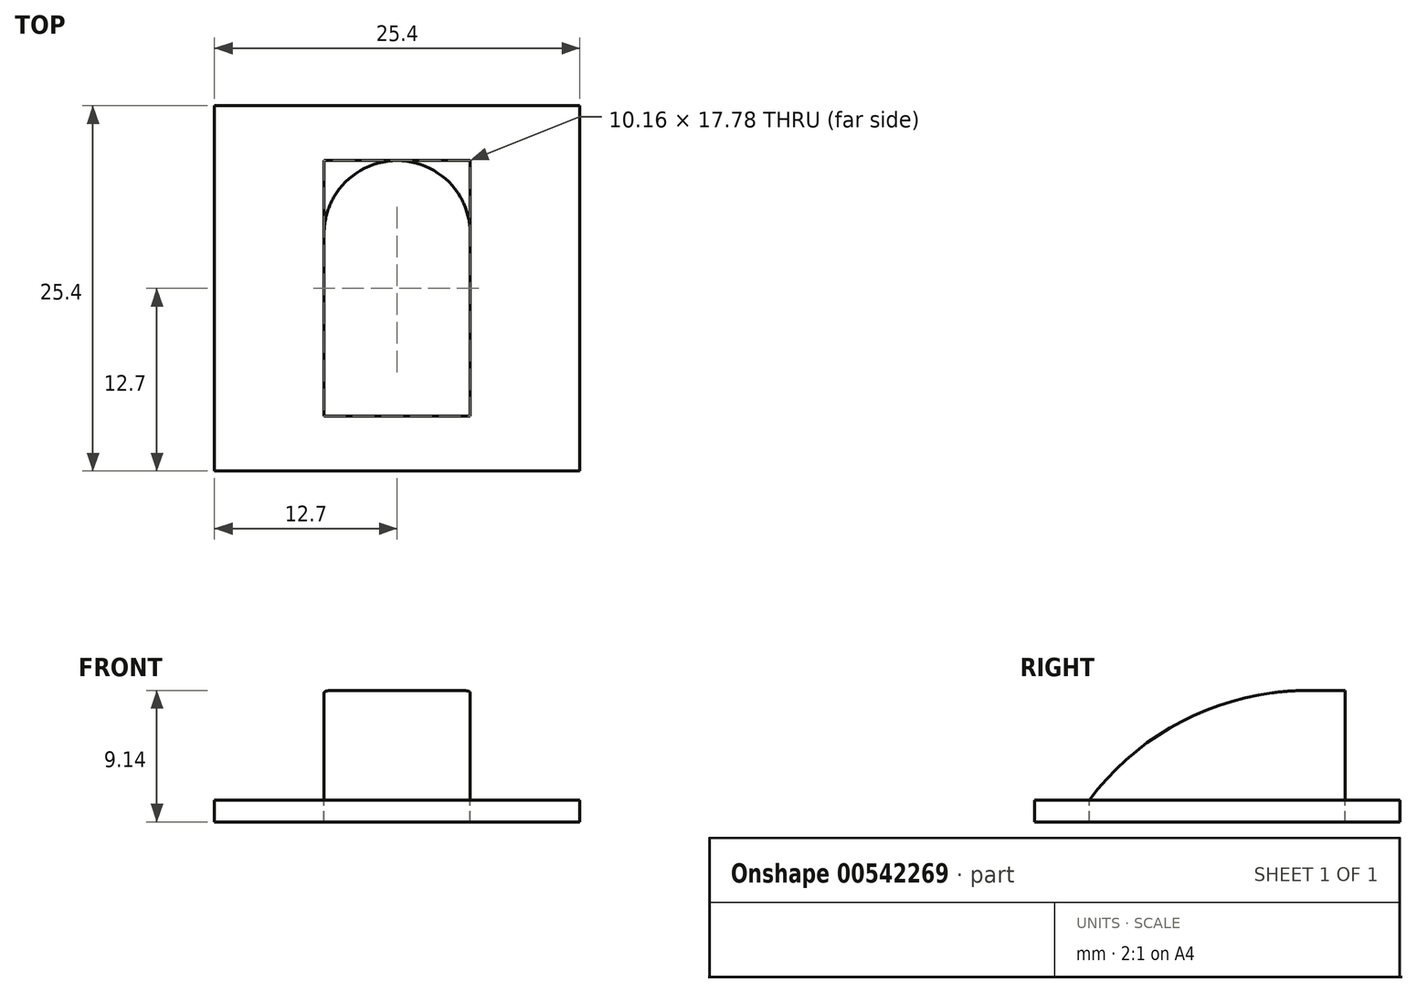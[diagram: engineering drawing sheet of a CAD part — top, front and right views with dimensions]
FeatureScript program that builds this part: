
annotation { "Feature Type Name" : "Feature", "Feature Type Description" : "" }
export const myFeature = defineFeature(function(context is Context, id is Id, definition is map)
    precondition{}
    {
        {
            var Q0;
            Q0=qCreatedBy(makeId("Top.planeOp"),FACE);
            var sketch = newSketch(context, id + "F0", { "sketchPlane" : qUnion([Q0])});
            skLineSegment(sketch, "E0.bottom", {"start": v(-25.4, 0) * mm, "end": v(0, 0) * mm});
            skLineSegment(sketch, "E0.top", {"start": v(-25.4, 25.4) * mm, "end": v(0, 25.4) * mm});
            skLineSegment(sketch, "E0.left", {"start": v(-25.4, 0) * mm, "end": v(-25.4, 25.4) * mm});
            skLineSegment(sketch, "E0.right", {"start": v(0, 0) * mm, "end": v(0, 25.4) * mm});
            skLineSegment(sketch, "E1.bottom", {"start": v(-17.78, 3.8) * mm, "end": v(-7.62, 3.81) * mm});
            skLineSegment(sketch, "E1.top", {"start": v(-17.78, 21.59) * mm, "end": v(-7.62, 21.59) * mm});
            skLineSegment(sketch, "E1.left", {"start": v(-17.78, 3.81) * mm, "end": v(-17.78, 21.59) * mm});
            skLineSegment(sketch, "E1.right", {"start": v(-7.62, 3.81) * mm, "end": v(-7.62, 21.59) * mm});
            skSolve(sketch);
        }
        {
            var Q0;
            Q0=makeQuery(id+"F0.imprint","IMPRINT",FACE,{"disambiguationData":[TD([[makeQuery(id+"F0.imprint","IMPRINT",EDGE,{"derivedFrom":sQuery(id+"F0.wireOp",EDGE,"E1.bottom")}),1.0]])]});
            extrude(context, id + "F1", {"entities" : qUnion([Q0]), "depth" : 7.62 * mm, "offsetDistance" : 25.4 * mm});
        }
        {
            var Q0;
            Q0=makeQuery(id+"F1.opExtrude","CAP_EDGE",EDGE,{"disambiguationData":[OSD([sQuery(id+"F0.wireOp",EDGE,"E1.bottom")])],"isStart":false});
            fillet(context, id + "F2", {"entities" : qUnion([Q0]), "radius" : 19 * mm, "tangentPropagation" : true, "allowEdgeOverflow" : false});
        }
        {
            var Q0;
            Q0=makeQuery(id+"F1.opExtrude","SWEPT_EDGE",EDGE,{"disambiguationData":[OSD([sQuery(id+"F0.wireOp",EDGE,"E1.top"),sQuery(id+"F0.wireOp",EDGE,"E1.left")])]});
            var Q1;
            Q1=makeQuery(id+"F1.opExtrude","SWEPT_EDGE",EDGE,{"disambiguationData":[OSD([sQuery(id+"F0.wireOp",EDGE,"E1.top"),sQuery(id+"F0.wireOp",EDGE,"E1.right")])]});
            fillet(context, id + "F3", {"entities" : qUnion([Q0, Q1]), "radius" : 5.08 * mm, "tangentPropagation" : true, "allowEdgeOverflow" : false});
        }
        {
            var Q0;
            Q0 = qSketchRegion(id + "F0", true);
            extrude(context, id + "F4", {"entities" : qUnion([Q0]), "oppositeDirection" : true, "depth" : 1.52 * mm, "offsetDistance" : 25.4 * mm});
        }
    });
